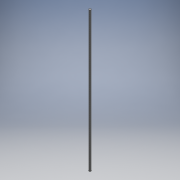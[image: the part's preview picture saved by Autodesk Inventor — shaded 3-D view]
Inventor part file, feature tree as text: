
AUTODESK INVENTOR PART (.ipt)
format: ipt  version: 2018 (Build 220112000, 112)  size: 93,184 bytes
history: native  units: mm
features: sketch x2, extrude x1, thread x1
ambient origin geometry x8: Origin, YZ Plane, XZ Plane, XY Plane, X Axis, Y Axis, Z Axis, Center Point
bodies: Solid1 (feature_tree)
feature tree (4):
  sketch  "Sketch1"  dims[d0=6.0mm d1=398.0mm d2=0.0mm d3=10.0mm d4=0.0mm]
  extrude  "Extrusion1"  Depth=398.0mm TaperAngle=0.0deg
  thread  "Thread1"  [1 undecoded]
  sketch  "Sketch2"
note: 1 required parameter value undecoded (feature->parameter linkage not recoverable at this tier; creation-order binding heuristic only, values carry confidence <= 0.55)
